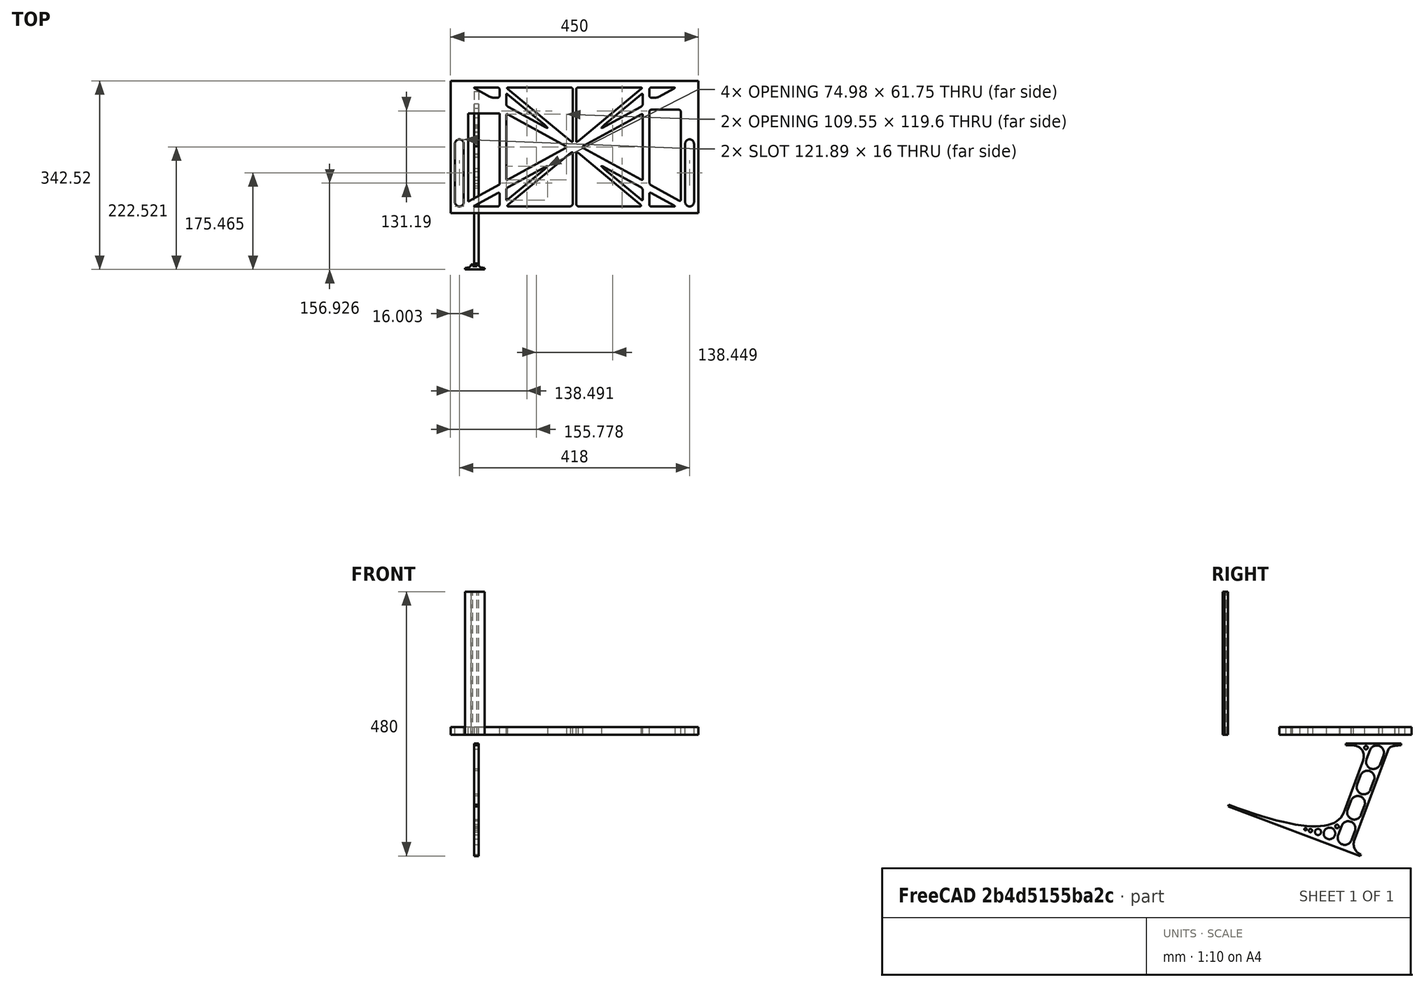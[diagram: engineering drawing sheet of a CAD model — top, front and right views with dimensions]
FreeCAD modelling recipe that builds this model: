
FCSTD DOCUMENT  (FreeCAD 0.19R0.19.2)
Label: laptopStand127FCStd
License: All rights reserved
LicenseURL: http://en.wikipedia.org/wiki/All_rights_reserved
objects: Sketcher::SketchObject×3, Part::Extrusion×3
note: 6 computed .brp shape members not serialized (recipe doc carries the construction recipe); baked Part::Feature solids carry a one-line shape summary decoded from their .brp

FEATURE [Sketcher::SketchObject] Sketch
  FullyConstrained = true
  sketch-geometry (352):
    g0: LineSegment StartX=-10.9272 StartY=-82.7794 StartZ=0 EndX=46.0728 EndY=-51.4823 EndZ=0
    g1: LineSegment StartX=-10.9272 StartY=76.4095 StartZ=0 EndX=-10.9272 EndY=-82.7794 EndZ=0
    g2: LineSegment StartX=46.0728 StartY=76.4095 StartZ=0 EndX=46.0728 EndY=-51.4823 EndZ=0
    g3: LineSegment StartX=-42.9272 StartY=136.221 StartZ=0 EndX=-42.9272 EndY=-103.779 EndZ=0
    g4: LineSegment StartX=407.073 StartY=136.221 StartZ=0 EndX=407.073 EndY=-103.779 EndZ=0
    g5: ArcOfCircle CenterX=-26.9272 CenterY=22.1087 CenterZ=0 NormalX=0 NormalY=0 NormalZ=1 AngleXU=0 Radius=8 StartAngle=1e-16 EndAngle=3.14159
    g6: ArcOfCircle CenterX=-26.9272 CenterY=-83.7794 CenterZ=0 NormalX=0 NormalY=0 NormalZ=1 AngleXU=0 Radius=8 StartAngle=3.14159 EndAngle=6.28319
    g7: LineSegment StartX=-34.9272 StartY=22.1087 StartZ=0 EndX=-34.9272 EndY=-83.7794 EndZ=0
    g8: LineSegment StartX=-18.9272 StartY=22.1087 StartZ=0 EndX=-18.9272 EndY=-83.7794 EndZ=0
    g9: ArcOfCircle CenterX=391.073 CenterY=22.1087 CenterZ=0 NormalX=0 NormalY=0 NormalZ=1 AngleXU=0 Radius=8 StartAngle=-4.4e-15 EndAngle=3.14159
    g10: LineSegment StartX=399.073 StartY=22.1087 StartZ=0 EndX=399.073 EndY=-83.7794 EndZ=0
    g11: LineSegment StartX=383.073 StartY=22.1087 StartZ=0 EndX=383.073 EndY=-83.7794 EndZ=0
    g12: ArcOfCircle CenterX=391.073 CenterY=-83.7794 CenterZ=0 NormalX=0 NormalY=0 NormalZ=1 AngleXU=0 Radius=8 StartAngle=3.14159 EndAngle=6.28319
    g13: Circle CenterX=175.022 CenterY=27.0628 CenterZ=0 NormalX=0 NormalY=0 NormalZ=1 AngleXU=0 Radius=1
    g14: Circle CenterX=179.022 CenterY=24.8665 CenterZ=0 NormalX=0 NormalY=0 NormalZ=1 AngleXU=0 Radius=1
    g15: Circle CenterX=179.022 CenterY=27.0628 CenterZ=0 NormalX=0 NormalY=0 NormalZ=1 AngleXU=0 Radius=1
    g16: BSplineCurve PolesCount=3 KnotsCount=2 Degree=2 IsPeriodic=0
    g17: GeomPoint X=175.022 Y=27.0628 Z=0
    g18: GeomPoint X=179.022 Y=27.0628 Z=0
    g19: Circle CenterX=189.124 CenterY=27.0628 CenterZ=0 NormalX=0 NormalY=0 NormalZ=1 AngleXU=0 Radius=1
    g20: Circle CenterX=185.124 CenterY=24.8665 CenterZ=0 NormalX=0 NormalY=0 NormalZ=1 AngleXU=0 Radius=1
    g21: Circle CenterX=185.124 CenterY=27.0628 CenterZ=0 NormalX=0 NormalY=0 NormalZ=1 AngleXU=0 Radius=1
    g22: BSplineCurve PolesCount=3 KnotsCount=2 Degree=2 IsPeriodic=0
    g23: GeomPoint X=189.124 Y=27.0628 Z=0
    g24: GeomPoint X=185.124 Y=27.0628 Z=0
    g25: Circle CenterX=175.022 CenterY=5.37834 CenterZ=0 NormalX=0 NormalY=0 NormalZ=1 AngleXU=0 Radius=1
    g26: Circle CenterX=179.022 CenterY=7.57463 CenterZ=0 NormalX=0 NormalY=0 NormalZ=1 AngleXU=0 Radius=1
    g27: Circle CenterX=179.022 CenterY=5.34704 CenterZ=0 NormalX=0 NormalY=0 NormalZ=1 AngleXU=0 Radius=1
    g28: BSplineCurve PolesCount=3 KnotsCount=2 Degree=2 IsPeriodic=0
    g29: GeomPoint X=175.022 Y=5.37834 Z=0
    g30: GeomPoint X=179.022 Y=5.34704 Z=0
    g31: Circle CenterX=189.124 CenterY=5.37834 CenterZ=0 NormalX=0 NormalY=0 NormalZ=1 AngleXU=0 Radius=1
    g32: Circle CenterX=185.124 CenterY=7.57463 CenterZ=0 NormalX=0 NormalY=0 NormalZ=1 AngleXU=0 Radius=1
    g33: Circle CenterX=185.124 CenterY=5.34704 CenterZ=0 NormalX=0 NormalY=0 NormalZ=1 AngleXU=0 Radius=1
    g34: BSplineCurve PolesCount=3 KnotsCount=2 Degree=2 IsPeriodic=0
    g35: GeomPoint X=189.124 Y=5.37834 Z=0
    g36: GeomPoint X=185.124 Y=5.34704 Z=0
    g37: Circle CenterX=165.871 CenterY=18.1458 CenterZ=0 NormalX=0 NormalY=0 NormalZ=1 AngleXU=0 Radius=1
    g38: Circle CenterX=169.377 CenterY=16.2206 CenterZ=0 NormalX=0 NormalY=0 NormalZ=1 AngleXU=0 Radius=1
    g39: Circle CenterX=165.871 CenterY=14.2954 CenterZ=0 NormalX=0 NormalY=0 NormalZ=1 AngleXU=0 Radius=1
    g40: BSplineCurve PolesCount=3 KnotsCount=2 Degree=2 IsPeriodic=0
    g41: GeomPoint X=165.871 Y=18.1458 Z=0
    g42: GeomPoint X=165.871 Y=14.2954 Z=0
    g43: Circle CenterX=198.275 CenterY=18.1458 CenterZ=0 NormalX=0 NormalY=0 NormalZ=1 AngleXU=0 Radius=1
    g44: Circle CenterX=194.768 CenterY=16.2206 CenterZ=0 NormalX=0 NormalY=0 NormalZ=1 AngleXU=0 Radius=1
    g45: Circle CenterX=198.275 CenterY=14.2954 CenterZ=0 NormalX=0 NormalY=0 NormalZ=1 AngleXU=0 Radius=1
    g46: BSplineCurve PolesCount=3 KnotsCount=2 Degree=2 IsPeriodic=0
    g47: GeomPoint X=198.275 Y=18.1458 Z=0
    g48: GeomPoint X=198.275 Y=14.2954 Z=0
    g49: LineSegment StartX=407.073 StartY=-103.779 StartZ=0 EndX=-42.9272 EndY=-103.779 EndZ=0
    g50: LineSegment StartX=407.073 StartY=136.221 StartZ=0 EndX=-42.9272 EndY=136.221 EndZ=0
    g51: LineSegment StartX=46.0728 StartY=76.4095 StartZ=0 EndX=-10.9272 EndY=76.4095 EndZ=0
    g52: Circle CenterX=125.607 CenterY=54.1951 CenterZ=0 NormalX=0 NormalY=0 NormalZ=1 AngleXU=0 Radius=1
    g53: Circle CenterX=139.632 CenterY=46.4944 CenterZ=0 NormalX=0 NormalY=0 NormalZ=1 AngleXU=0 Radius=1
    g54: Circle CenterX=127.326 CenterY=56.7187 CenterZ=0 NormalX=0 NormalY=0 NormalZ=1 AngleXU=0 Radius=1
    g55: BSplineCurve PolesCount=3 KnotsCount=2 Degree=2 IsPeriodic=0
    g56: GeomPoint X=125.607 Y=54.1951 Z=0
    g57: GeomPoint X=127.326 Y=56.7187 Z=0
    g58: Circle CenterX=236.821 CenterY=56.7187 CenterZ=0 NormalX=0 NormalY=0 NormalZ=1 AngleXU=0 Radius=1
    g59: Circle CenterX=224.513 CenterY=46.4944 CenterZ=0 NormalX=0 NormalY=0 NormalZ=1 AngleXU=0 Radius=1
    g60: Circle CenterX=238.538 CenterY=54.1951 CenterZ=0 NormalX=0 NormalY=0 NormalZ=1 AngleXU=0 Radius=1
    g61: BSplineCurve PolesCount=3 KnotsCount=2 Degree=2 IsPeriodic=0
    g62: GeomPoint X=236.821 Y=56.7187 Z=0
    g63: GeomPoint X=238.538 Y=54.1951 Z=0
    g64: Circle CenterX=238.538 CenterY=-21.7539 CenterZ=0 NormalX=0 NormalY=0 NormalZ=1 AngleXU=0 Radius=1
    g65: Circle CenterX=224.513 CenterY=-14.0532 CenterZ=0 NormalX=0 NormalY=0 NormalZ=1 AngleXU=0 Radius=1
    g66: Circle CenterX=236.821 CenterY=-24.2775 CenterZ=0 NormalX=0 NormalY=0 NormalZ=1 AngleXU=0 Radius=1
    g67: BSplineCurve PolesCount=3 KnotsCount=2 Degree=2 IsPeriodic=0
    g68: GeomPoint X=238.538 Y=-21.7539 Z=0
    g69: GeomPoint X=236.821 Y=-24.2775 Z=0
    g70: Circle CenterX=125.607 CenterY=-21.7539 CenterZ=0 NormalX=0 NormalY=0 NormalZ=1 AngleXU=0 Radius=1
    g71: Circle CenterX=139.632 CenterY=-14.0532 CenterZ=0 NormalX=0 NormalY=0 NormalZ=1 AngleXU=0 Radius=1
    g72: Circle CenterX=127.325 CenterY=-24.2775 CenterZ=0 NormalX=0 NormalY=0 NormalZ=1 AngleXU=0 Radius=1
    g73: BSplineCurve PolesCount=3 KnotsCount=2 Degree=2 IsPeriodic=0
    g74: GeomPoint X=125.607 Y=-21.7539 Z=0
    g75: GeomPoint X=127.325 Y=-24.2775 Z=0
    g76: Circle CenterX=302.996 CenterY=111.695 CenterZ=0 NormalX=0 NormalY=0 NormalZ=1 AngleXU=0 Radius=1
    g77: Circle CenterX=306.073 CenterY=114.251 CenterZ=0 NormalX=0 NormalY=0 NormalZ=1 AngleXU=0 Radius=1
    g78: Circle CenterX=306.073 CenterY=110.251 CenterZ=0 NormalX=0 NormalY=0 NormalZ=1 AngleXU=0 Radius=1
    g79: BSplineCurve PolesCount=3 KnotsCount=2 Degree=2 IsPeriodic=0
    g80: GeomPoint X=302.996 Y=111.695 Z=0
    g81: GeomPoint X=306.073 Y=110.251 Z=0
    g82: Circle CenterX=306.073 CenterY=95.2763 CenterZ=0 NormalX=0 NormalY=0 NormalZ=1 AngleXU=0 Radius=1
    g83: Circle CenterX=306.073 CenterY=91.2763 CenterZ=0 NormalX=0 NormalY=0 NormalZ=1 AngleXU=0 Radius=1
    g84: Circle CenterX=302.567 CenterY=89.3511 CenterZ=0 NormalX=0 NormalY=0 NormalZ=1 AngleXU=0 Radius=1
    g85: BSplineCurve PolesCount=3 KnotsCount=2 Degree=2 IsPeriodic=0
    g86: GeomPoint X=306.073 Y=95.2763 Z=0
    g87: GeomPoint X=302.567 Y=89.3511 Z=0
    g88: LineSegment StartX=306.073 StartY=110.251 StartZ=0 EndX=306.073 EndY=95.2763 EndZ=0
    g89: LineSegment StartX=302.996 StartY=111.695 StartZ=0 EndX=236.821 EndY=56.7187 EndZ=0
    g90: LineSegment StartX=238.538 StartY=54.1951 StartZ=0 EndX=302.567 EndY=89.3511 EndZ=0
    g91: Circle CenterX=61.1496 CenterY=111.695 CenterZ=0 NormalX=0 NormalY=0 NormalZ=1 AngleXU=0 Radius=1
    g92: Circle CenterX=58.0728 CenterY=114.251 CenterZ=0 NormalX=0 NormalY=0 NormalZ=1 AngleXU=0 Radius=1
    g93: Circle CenterX=58.0728 CenterY=110.251 CenterZ=0 NormalX=0 NormalY=0 NormalZ=1 AngleXU=0 Radius=1
    g94: BSplineCurve PolesCount=3 KnotsCount=2 Degree=2 IsPeriodic=0
    g95: GeomPoint X=61.1496 Y=111.695 Z=0
    g96: GeomPoint X=58.0728 Y=110.251 Z=0
    g97: Circle CenterX=61.5791 CenterY=89.3511 CenterZ=0 NormalX=0 NormalY=0 NormalZ=1 AngleXU=0 Radius=1
    g98: Circle CenterX=58.0728 CenterY=91.2763 CenterZ=0 NormalX=0 NormalY=0 NormalZ=1 AngleXU=0 Radius=1
    g99: Circle CenterX=58.0728 CenterY=95.2763 CenterZ=0 NormalX=0 NormalY=0 NormalZ=1 AngleXU=0 Radius=1
    g100: BSplineCurve PolesCount=3 KnotsCount=2 Degree=2 IsPeriodic=0
    g101: GeomPoint X=61.5791 Y=89.3511 Z=0
    g102: GeomPoint X=58.0728 Y=95.2763 Z=0
    g103: LineSegment StartX=58.0728 StartY=110.251 StartZ=0 EndX=58.0728 EndY=95.2763 EndZ=0
    g104: LineSegment StartX=61.1496 StartY=111.695 StartZ=0 EndX=127.326 EndY=56.7187 EndZ=0
    g105: LineSegment StartX=125.607 StartY=54.1951 StartZ=0 EndX=61.5791 EndY=89.3511 EndZ=0
    g106: Circle CenterX=61.5791 CenterY=-56.9099 CenterZ=0 NormalX=0 NormalY=0 NormalZ=1 AngleXU=0 Radius=1
    g107: Circle CenterX=58.0728 CenterY=-58.8351 CenterZ=0 NormalX=0 NormalY=0 NormalZ=1 AngleXU=0 Radius=1
    g108: Circle CenterX=58.0728 CenterY=-62.8351 CenterZ=0 NormalX=0 NormalY=0 NormalZ=1 AngleXU=0 Radius=1
    g109: BSplineCurve PolesCount=3 KnotsCount=2 Degree=2 IsPeriodic=0
    g110: GeomPoint X=61.5791 Y=-56.9099 Z=0
    g111: GeomPoint X=58.0728 Y=-62.8351 Z=0
    g112: Circle CenterX=58.0728 CenterY=-77.8102 CenterZ=0 NormalX=0 NormalY=0 NormalZ=1 AngleXU=0 Radius=1
    g113: Circle CenterX=58.0728 CenterY=-81.8102 CenterZ=0 NormalX=0 NormalY=0 NormalZ=1 AngleXU=0 Radius=1
    g114: Circle CenterX=61.1496 CenterY=-79.2541 CenterZ=0 NormalX=0 NormalY=0 NormalZ=1 AngleXU=0 Radius=1
    g115: BSplineCurve PolesCount=3 KnotsCount=2 Degree=2 IsPeriodic=0
    g116: GeomPoint X=58.0728 Y=-77.8102 Z=0
    g117: GeomPoint X=61.1496 Y=-79.2541 Z=0
    g118: LineSegment StartX=58.0728 StartY=-62.8351 StartZ=0 EndX=58.0728 EndY=-77.8102 EndZ=0
    g119: LineSegment StartX=61.1496 StartY=-79.2541 StartZ=0 EndX=127.325 EndY=-24.2775 EndZ=0
    g120: LineSegment StartX=125.607 StartY=-21.7539 StartZ=0 EndX=61.5791 EndY=-56.9099 EndZ=0
    g121: Circle CenterX=302.567 CenterY=-56.9099 CenterZ=0 NormalX=0 NormalY=0 NormalZ=1 AngleXU=0 Radius=1
    g122: Circle CenterX=306.073 CenterY=-58.8351 CenterZ=0 NormalX=0 NormalY=0 NormalZ=1 AngleXU=0 Radius=1
    g123: Circle CenterX=306.073 CenterY=-62.8351 CenterZ=0 NormalX=0 NormalY=0 NormalZ=1 AngleXU=0 Radius=1
    g124: BSplineCurve PolesCount=3 KnotsCount=2 Degree=2 IsPeriodic=0
    g125: GeomPoint X=302.567 Y=-56.9099 Z=0
    g126: GeomPoint X=306.073 Y=-62.8351 Z=0
    g127: Circle CenterX=302.996 CenterY=-79.2541 CenterZ=0 NormalX=0 NormalY=0 NormalZ=1 AngleXU=0 Radius=1
    g128: Circle CenterX=306.073 CenterY=-81.8102 CenterZ=0 NormalX=0 NormalY=0 NormalZ=1 AngleXU=0 Radius=1
    g129: Circle CenterX=306.073 CenterY=-77.8102 CenterZ=0 NormalX=0 NormalY=0 NormalZ=1 AngleXU=0 Radius=1
    g130: BSplineCurve PolesCount=3 KnotsCount=2 Degree=2 IsPeriodic=0
    g131: GeomPoint X=302.996 Y=-79.2541 Z=0
    g132: GeomPoint X=306.073 Y=-77.8102 Z=0
    g133: LineSegment StartX=306.073 StartY=-62.8351 StartZ=0 EndX=306.073 EndY=-77.8102 EndZ=0
    g134: LineSegment StartX=302.996 StartY=-79.2541 StartZ=0 EndX=236.821 EndY=-24.2775 EndZ=0
    g135: LineSegment StartX=238.538 StartY=-21.7539 StartZ=0 EndX=302.567 EndY=-56.9099 EndZ=0
    g136: Circle CenterX=61.6457 CenterY=-88.8112 CenterZ=0 NormalX=0 NormalY=0 NormalZ=1 AngleXU=0 Radius=1
    g137: Circle CenterX=58.0728 CenterY=-91.7794 CenterZ=0 NormalX=0 NormalY=0 NormalZ=1 AngleXU=0 Radius=1
    g138: Circle CenterX=63.9135 CenterY=-91.7794 CenterZ=0 NormalX=0 NormalY=0 NormalZ=1 AngleXU=0 Radius=1
    g139: BSplineCurve PolesCount=3 KnotsCount=2 Degree=2 IsPeriodic=0
    g140: GeomPoint X=61.6457 Y=-88.8112 Z=0
    g141: GeomPoint X=63.9135 Y=-91.7794 Z=0
    g142: Circle CenterX=179.022 CenterY=-85.8163 CenterZ=0 NormalX=0 NormalY=0 NormalZ=1 AngleXU=0 Radius=1
    g143: Circle CenterX=179.022 CenterY=-91.7794 CenterZ=0 NormalX=0 NormalY=0 NormalZ=1 AngleXU=0 Radius=1
    g144: Circle CenterX=171.895 CenterY=-91.7794 CenterZ=0 NormalX=0 NormalY=0 NormalZ=1 AngleXU=0 Radius=1
    g145: BSplineCurve PolesCount=3 KnotsCount=2 Degree=2 IsPeriodic=0
    g146: GeomPoint X=179.022 Y=-85.8163 Z=0
    g147: GeomPoint X=171.895 Y=-91.7794 Z=0
    g148: Circle CenterX=185.124 CenterY=-86.2028 CenterZ=0 NormalX=0 NormalY=0 NormalZ=1 AngleXU=0 Radius=1
    g149: Circle CenterX=185.124 CenterY=-91.7794 CenterZ=0 NormalX=0 NormalY=0 NormalZ=1 AngleXU=0 Radius=1
    g150: Circle CenterX=191.747 CenterY=-91.7794 CenterZ=0 NormalX=0 NormalY=0 NormalZ=1 AngleXU=0 Radius=1
    g151: BSplineCurve PolesCount=3 KnotsCount=2 Degree=2 IsPeriodic=0
    g152: GeomPoint X=185.124 Y=-86.2028 Z=0
    g153: GeomPoint X=191.747 Y=-91.7794 Z=0
    g154: Circle CenterX=299.888 CenterY=-86.6413 CenterZ=0 NormalX=0 NormalY=0 NormalZ=1 AngleXU=0 Radius=1
    g155: Circle CenterX=306.073 CenterY=-91.7794 CenterZ=0 NormalX=0 NormalY=0 NormalZ=1 AngleXU=0 Radius=1
    g156: Circle CenterX=298.776 CenterY=-91.7794 CenterZ=0 NormalX=0 NormalY=0 NormalZ=1 AngleXU=0 Radius=1
    g157: BSplineCurve PolesCount=3 KnotsCount=2 Degree=2 IsPeriodic=0
    g158: GeomPoint X=299.888 Y=-86.6413 Z=0
    g159: GeomPoint X=298.776 Y=-91.7794 Z=0
    g160: LineSegment StartX=189.124 StartY=5.37834 StartZ=0 EndX=299.888 EndY=-86.6413 EndZ=0
    g161: LineSegment StartX=298.776 StartY=-91.7794 StartZ=0 EndX=191.747 EndY=-91.7794 EndZ=0
    g162: LineSegment StartX=185.124 StartY=-86.2028 StartZ=0 EndX=185.124 EndY=5.34704 EndZ=0
    g163: LineSegment StartX=179.022 StartY=5.34704 StartZ=0 EndX=179.022 EndY=-85.8163 EndZ=0
    g164: LineSegment StartX=171.895 StartY=-91.7794 StartZ=0 EndX=63.9135 EndY=-91.7794 EndZ=0
    g165: LineSegment StartX=61.6457 StartY=-88.8112 StartZ=0 EndX=175.022 EndY=5.37834 EndZ=0
    g166: Circle CenterX=302.073 CenterY=124.221 CenterZ=0 NormalX=0 NormalY=0 NormalZ=1 AngleXU=0 Radius=1
    g167: Circle CenterX=306.073 CenterY=124.221 CenterZ=0 NormalX=0 NormalY=0 NormalZ=1 AngleXU=0 Radius=1
    g168: Circle CenterX=302.996 CenterY=121.665 CenterZ=0 NormalX=0 NormalY=0 NormalZ=1 AngleXU=0 Radius=1
    g169: BSplineCurve PolesCount=3 KnotsCount=2 Degree=2 IsPeriodic=0
    g170: GeomPoint X=302.073 Y=124.221 Z=0
    g171: GeomPoint X=302.996 Y=121.665 Z=0
    g172: Circle CenterX=189.124 CenterY=124.221 CenterZ=0 NormalX=0 NormalY=0 NormalZ=1 AngleXU=0 Radius=1
    g173: Circle CenterX=185.124 CenterY=124.221 CenterZ=0 NormalX=0 NormalY=0 NormalZ=1 AngleXU=0 Radius=1
    g174: Circle CenterX=185.124 CenterY=120.221 CenterZ=0 NormalX=0 NormalY=0 NormalZ=1 AngleXU=0 Radius=1
    g175: BSplineCurve PolesCount=3 KnotsCount=2 Degree=2 IsPeriodic=0
    g176: GeomPoint X=189.124 Y=124.221 Z=0
    g177: GeomPoint X=185.124 Y=120.221 Z=0
    g178: Circle CenterX=175.022 CenterY=124.221 CenterZ=0 NormalX=0 NormalY=0 NormalZ=1 AngleXU=0 Radius=1
    g179: Circle CenterX=179.022 CenterY=124.221 CenterZ=0 NormalX=0 NormalY=0 NormalZ=1 AngleXU=0 Radius=1
    g180: Circle CenterX=179.022 CenterY=120.221 CenterZ=0 NormalX=0 NormalY=0 NormalZ=1 AngleXU=0 Radius=1
    g181: BSplineCurve PolesCount=3 KnotsCount=2 Degree=2 IsPeriodic=0
    g182: GeomPoint X=175.022 Y=124.221 Z=0
    g183: GeomPoint X=179.022 Y=120.221 Z=0
    g184: Circle CenterX=62.0728 CenterY=124.221 CenterZ=0 NormalX=0 NormalY=0 NormalZ=1 AngleXU=0 Radius=1
    g185: Circle CenterX=58.0728 CenterY=124.221 CenterZ=0 NormalX=0 NormalY=0 NormalZ=1 AngleXU=0 Radius=1
    g186: Circle CenterX=61.1496 CenterY=121.665 CenterZ=0 NormalX=0 NormalY=0 NormalZ=1 AngleXU=0 Radius=1
    g187: BSplineCurve PolesCount=3 KnotsCount=2 Degree=2 IsPeriodic=0
    g188: GeomPoint X=62.0728 Y=124.221 Z=0
    g189: GeomPoint X=61.1496 Y=121.665 Z=0
    g190: LineSegment StartX=62.0728 StartY=124.221 StartZ=0 EndX=175.022 EndY=124.221 EndZ=0
    g191: LineSegment StartX=179.022 StartY=120.221 StartZ=0 EndX=179.022 EndY=27.0628 EndZ=0
    g192: LineSegment StartX=185.124 StartY=27.0628 StartZ=0 EndX=185.124 EndY=120.221 EndZ=0
    g193: LineSegment StartX=189.124 StartY=124.221 StartZ=0 EndX=302.073 EndY=124.221 EndZ=0
    g194: LineSegment StartX=302.996 StartY=121.665 StartZ=0 EndX=189.124 EndY=27.0628 EndZ=0
    g195: LineSegment StartX=175.022 StartY=27.0628 StartZ=0 EndX=61.1496 EndY=121.665 EndZ=0
    g196: Circle CenterX=61.5791 CenterY=75.4095 CenterZ=0 NormalX=0 NormalY=0 NormalZ=1 AngleXU=0 Radius=1
    g197: Circle CenterX=58.0728 CenterY=77.3346 CenterZ=0 NormalX=0 NormalY=0 NormalZ=1 AngleXU=0 Radius=1
    g198: Circle CenterX=58.0728 CenterY=73.3346 CenterZ=0 NormalX=0 NormalY=0 NormalZ=1 AngleXU=0 Radius=1
    g199: BSplineCurve PolesCount=3 KnotsCount=2 Degree=2 IsPeriodic=0
    g200: GeomPoint X=61.5791 Y=75.4095 Z=0
    g201: GeomPoint X=58.0728 Y=73.3346 Z=0
    g202: Circle CenterX=58.0728 CenterY=-40.8935 CenterZ=0 NormalX=0 NormalY=0 NormalZ=1 AngleXU=0 Radius=1
    g203: Circle CenterX=58.0728 CenterY=-44.8935 CenterZ=0 NormalX=0 NormalY=0 NormalZ=1 AngleXU=0 Radius=1
    g204: Circle CenterX=61.5791 CenterY=-42.9683 CenterZ=0 NormalX=0 NormalY=0 NormalZ=1 AngleXU=0 Radius=1
    g205: BSplineCurve PolesCount=3 KnotsCount=2 Degree=2 IsPeriodic=0
    g206: GeomPoint X=58.0728 Y=-40.8935 Z=0
    g207: GeomPoint X=61.5791 Y=-42.9683 Z=0
    g208: LineSegment StartX=61.5791 StartY=-42.9683 StartZ=0 EndX=165.871 EndY=14.2954 EndZ=0
    g209: LineSegment StartX=165.871 StartY=18.1458 StartZ=0 EndX=61.5791 EndY=75.4095 EndZ=0
    g210: LineSegment StartX=58.0728 StartY=73.3346 StartZ=0 EndX=58.0728 EndY=-40.8935 EndZ=0
    g211: Circle CenterX=302.567 CenterY=-42.9683 CenterZ=0 NormalX=0 NormalY=0 NormalZ=1 AngleXU=0 Radius=1
    g212: Circle CenterX=306.073 CenterY=-44.8935 CenterZ=0 NormalX=0 NormalY=0 NormalZ=1 AngleXU=0 Radius=1
    g213: Circle CenterX=306.073 CenterY=-40.8935 CenterZ=0 NormalX=0 NormalY=0 NormalZ=1 AngleXU=0 Radius=1
    g214: BSplineCurve PolesCount=3 KnotsCount=2 Degree=2 IsPeriodic=0
    g215: GeomPoint X=302.567 Y=-42.9683 Z=0
    g216: GeomPoint X=306.073 Y=-40.8935 Z=0
    g217: Circle CenterX=306.073 CenterY=73.3346 CenterZ=0 NormalX=0 NormalY=0 NormalZ=1 AngleXU=0 Radius=1
    g218: Circle CenterX=306.073 CenterY=77.3346 CenterZ=0 NormalX=0 NormalY=0 NormalZ=1 AngleXU=0 Radius=1
    g219: Circle CenterX=302.567 CenterY=75.4095 CenterZ=0 NormalX=0 NormalY=0 NormalZ=1 AngleXU=0 Radius=1
    g220: BSplineCurve PolesCount=3 KnotsCount=2 Degree=2 IsPeriodic=0
    g221: GeomPoint X=306.073 Y=73.3346 Z=0
    g222: GeomPoint X=302.567 Y=75.4095 Z=0
    g223: LineSegment StartX=302.567 StartY=-42.9683 StartZ=0 EndX=198.275 EndY=14.2954 EndZ=0
    g224: LineSegment StartX=198.275 StartY=18.1458 StartZ=0 EndX=302.567 EndY=75.4095 EndZ=0
    g225: LineSegment StartX=306.073 StartY=73.3346 StartZ=0 EndX=306.073 EndY=-40.8935 EndZ=0
    g226: LineSegment StartX=322.073 StartY=105.865 StartZ=0 EndX=328.643 EndY=105.865 EndZ=0
    g227: LineSegment StartX=318.073 StartY=120.221 StartZ=0 EndX=318.073 EndY=109.865 EndZ=0
    g228: LineSegment StartX=336.157 StartY=107.779 StartZ=0 EndX=362.567 EndY=122.294 EndZ=0
    g229: Circle CenterX=362.073 CenterY=124.221 CenterZ=0 NormalX=0 NormalY=0 NormalZ=1 AngleXU=0 Radius=1
    g230: Circle CenterX=366.073 CenterY=124.221 CenterZ=0 NormalX=0 NormalY=0 NormalZ=1 AngleXU=0 Radius=1
    g231: Circle CenterX=362.567 CenterY=122.294 CenterZ=0 NormalX=0 NormalY=0 NormalZ=1 AngleXU=0 Radius=1
    g232: BSplineCurve PolesCount=3 KnotsCount=2 Degree=2 IsPeriodic=0
    g233: GeomPoint X=362.073 Y=124.221 Z=0
    g234: GeomPoint X=362.567 Y=122.294 Z=0
    g235: Circle CenterX=322.073 CenterY=124.221 CenterZ=0 NormalX=0 NormalY=0 NormalZ=1 AngleXU=0 Radius=1
    g236: Circle CenterX=318.073 CenterY=124.221 CenterZ=0 NormalX=0 NormalY=0 NormalZ=1 AngleXU=0 Radius=1
    g237: Circle CenterX=318.073 CenterY=120.221 CenterZ=0 NormalX=0 NormalY=0 NormalZ=1 AngleXU=0 Radius=1
    g238: BSplineCurve PolesCount=3 KnotsCount=2 Degree=2 IsPeriodic=0
    g239: GeomPoint X=322.073 Y=124.221 Z=0
    g240: GeomPoint X=318.073 Y=120.221 Z=0
    g241: Circle CenterX=322.073 CenterY=105.865 CenterZ=0 NormalX=0 NormalY=0 NormalZ=1 AngleXU=0 Radius=1
    g242: Circle CenterX=318.073 CenterY=105.865 CenterZ=0 NormalX=0 NormalY=0 NormalZ=1 AngleXU=0 Radius=1
    g243: Circle CenterX=318.073 CenterY=109.865 CenterZ=0 NormalX=0 NormalY=0 NormalZ=1 AngleXU=0 Radius=1
    g244: BSplineCurve PolesCount=3 KnotsCount=2 Degree=2 IsPeriodic=0
    g245: GeomPoint X=322.073 Y=105.865 Z=0
    g246: GeomPoint X=318.073 Y=109.865 Z=0
    g247: Circle CenterX=336.157 CenterY=107.779 CenterZ=0 NormalX=0 NormalY=0 NormalZ=1 AngleXU=0 Radius=1
    g248: Circle CenterX=332.651 CenterY=105.853 CenterZ=0 NormalX=0 NormalY=0 NormalZ=1 AngleXU=0 Radius=1
    g249: Circle CenterX=328.643 CenterY=105.865 CenterZ=0 NormalX=0 NormalY=0 NormalZ=1 AngleXU=0 Radius=1
    g250: BSplineCurve PolesCount=3 KnotsCount=2 Degree=2 IsPeriodic=0
    g251: GeomPoint X=336.157 Y=107.779 Z=0
    g252: GeomPoint X=328.643 Y=105.865 Z=0
    g253: LineSegment StartX=322.073 StartY=124.221 StartZ=0 EndX=362.073 EndY=124.221 EndZ=0
    g254: Circle CenterX=371.567 CenterY=-80.8644 CenterZ=0 NormalX=0 NormalY=0 NormalZ=1 AngleXU=0 Radius=1
    g255: Circle CenterX=375.073 CenterY=-82.7896 CenterZ=0 NormalX=0 NormalY=0 NormalZ=1 AngleXU=0 Radius=1
    g256: Circle CenterX=375.073 CenterY=-78.7896 CenterZ=0 NormalX=0 NormalY=0 NormalZ=1 AngleXU=0 Radius=1
    g257: BSplineCurve PolesCount=3 KnotsCount=2 Degree=2 IsPeriodic=0
    g258: GeomPoint X=371.567 Y=-80.8644 Z=0
    g259: GeomPoint X=375.073 Y=-78.7896 Z=0
    g260: Circle CenterX=321.579 CenterY=-53.4075 CenterZ=0 NormalX=0 NormalY=0 NormalZ=1 AngleXU=0 Radius=1
    g261: Circle CenterX=318.073 CenterY=-51.4823 CenterZ=0 NormalX=0 NormalY=0 NormalZ=1 AngleXU=0 Radius=1
    g262: Circle CenterX=318.073 CenterY=-47.4823 CenterZ=0 NormalX=0 NormalY=0 NormalZ=1 AngleXU=0 Radius=1
    g263: BSplineCurve PolesCount=3 KnotsCount=2 Degree=2 IsPeriodic=0
    g264: GeomPoint X=321.579 Y=-53.4075 Z=0
    g265: GeomPoint X=318.073 Y=-47.4823 Z=0
    g266: Circle CenterX=318.073 CenterY=79.9235 CenterZ=0 NormalX=0 NormalY=0 NormalZ=1 AngleXU=0 Radius=1
    g267: Circle CenterX=318.073 CenterY=83.9235 CenterZ=0 NormalX=0 NormalY=0 NormalZ=1 AngleXU=0 Radius=1
    g268: Circle CenterX=322.073 CenterY=83.9235 CenterZ=0 NormalX=0 NormalY=0 NormalZ=1 AngleXU=0 Radius=1
    g269: BSplineCurve PolesCount=3 KnotsCount=2 Degree=2 IsPeriodic=0
    g270: GeomPoint X=318.073 Y=79.9235 Z=0
    g271: GeomPoint X=322.073 Y=83.9235 Z=0
    g272: Circle CenterX=375.073 CenterY=79.9235 CenterZ=0 NormalX=0 NormalY=0 NormalZ=1 AngleXU=0 Radius=1
    g273: Circle CenterX=375.073 CenterY=83.9235 CenterZ=0 NormalX=0 NormalY=0 NormalZ=1 AngleXU=0 Radius=1
    g274: Circle CenterX=371.073 CenterY=83.9235 CenterZ=0 NormalX=0 NormalY=0 NormalZ=1 AngleXU=0 Radius=1
    g275: BSplineCurve PolesCount=3 KnotsCount=2 Degree=2 IsPeriodic=0
    g276: GeomPoint X=375.073 Y=79.9235 Z=0
    g277: GeomPoint X=371.073 Y=83.9235 Z=0
    g278: LineSegment StartX=322.073 StartY=83.9235 StartZ=0 EndX=371.073 EndY=83.9235 EndZ=0
    g279: LineSegment StartX=375.073 StartY=79.9235 StartZ=0 EndX=375.073 EndY=-78.7896 EndZ=0
    g280: LineSegment StartX=371.567 StartY=-80.8644 StartZ=0 EndX=321.579 EndY=-53.4075 EndZ=0
    g281: LineSegment StartX=318.073 StartY=-47.4823 StartZ=0 EndX=318.073 EndY=79.9235 EndZ=0
    g282: Circle CenterX=321.579 CenterY=-67.3492 CenterZ=0 NormalX=0 NormalY=0 NormalZ=1 AngleXU=0 Radius=1
    g283: Circle CenterX=318.073 CenterY=-65.424 CenterZ=0 NormalX=0 NormalY=0 NormalZ=1 AngleXU=0 Radius=1
    g284: Circle CenterX=318.073 CenterY=-69.424 CenterZ=0 NormalX=0 NormalY=0 NormalZ=1 AngleXU=0 Radius=1
    g285: BSplineCurve PolesCount=3 KnotsCount=2 Degree=2 IsPeriodic=0
    g286: GeomPoint X=321.579 Y=-67.3492 Z=0
    g287: GeomPoint X=318.073 Y=-69.424 Z=0
    g288: Circle CenterX=362.567 CenterY=-89.8542 CenterZ=0 NormalX=0 NormalY=0 NormalZ=1 AngleXU=0 Radius=1
    g289: Circle CenterX=366.073 CenterY=-91.7794 CenterZ=0 NormalX=0 NormalY=0 NormalZ=1 AngleXU=0 Radius=1
    g290: Circle CenterX=362.073 CenterY=-91.7794 CenterZ=0 NormalX=0 NormalY=0 NormalZ=1 AngleXU=0 Radius=1
    g291: BSplineCurve PolesCount=3 KnotsCount=2 Degree=2 IsPeriodic=0
    g292: GeomPoint X=362.567 Y=-89.8542 Z=0
    g293: GeomPoint X=362.073 Y=-91.7794 Z=0
    g294: Circle CenterX=322.073 CenterY=-91.7794 CenterZ=0 NormalX=0 NormalY=0 NormalZ=1 AngleXU=0 Radius=1
    g295: Circle CenterX=318.073 CenterY=-91.7794 CenterZ=0 NormalX=0 NormalY=0 NormalZ=1 AngleXU=0 Radius=1
    g296: Circle CenterX=318.073 CenterY=-87.7794 CenterZ=0 NormalX=0 NormalY=0 NormalZ=1 AngleXU=0 Radius=1
    g297: BSplineCurve PolesCount=3 KnotsCount=2 Degree=2 IsPeriodic=0
    g298: GeomPoint X=322.073 Y=-91.7794 Z=0
    g299: GeomPoint X=318.073 Y=-87.7794 Z=0
    g300: LineSegment StartX=362.567 StartY=-89.8542 StartZ=0 EndX=321.579 EndY=-67.3492 EndZ=0
    g301: LineSegment StartX=318.073 StartY=-69.424 StartZ=0 EndX=318.073 EndY=-87.7794 EndZ=0
    g302: LineSegment StartX=322.073 StartY=-91.7794 StartZ=0 EndX=362.073 EndY=-91.7794 EndZ=0
    g303: Circle CenterX=2.07281 CenterY=124.221 CenterZ=0 NormalX=0 NormalY=0 NormalZ=1 AngleXU=0 Radius=1
    g304: Circle CenterX=1.57905 CenterY=122.295 CenterZ=0 NormalX=0 NormalY=0 NormalZ=1 AngleXU=0 Radius=1
    g305: BSplineCurve PolesCount=3 KnotsCount=2 Degree=2 IsPeriodic=0
    g306: GeomPoint X=2.07281 Y=124.221 Z=0
    g307: GeomPoint X=1.57905 Y=122.295 Z=0
    g308: Circle CenterX=42.0728 CenterY=124.221 CenterZ=0 NormalX=0 NormalY=0 NormalZ=1 AngleXU=0 Radius=1
    g309: Circle CenterX=46.0728 CenterY=124.221 CenterZ=0 NormalX=0 NormalY=0 NormalZ=1 AngleXU=0 Radius=1
    g310: Circle CenterX=46.0728 CenterY=120.221 CenterZ=0 NormalX=0 NormalY=0 NormalZ=1 AngleXU=0 Radius=1
    g311: BSplineCurve PolesCount=3 KnotsCount=2 Degree=2 IsPeriodic=0
    g312: GeomPoint X=42.0728 Y=124.221 Z=0
    g313: GeomPoint X=46.0728 Y=120.221 Z=0
    g314: Circle CenterX=46.0728 CenterY=109.865 CenterZ=0 NormalX=0 NormalY=0 NormalZ=1 AngleXU=0 Radius=1
    g315: Circle CenterX=46.0728 CenterY=105.865 CenterZ=0 NormalX=0 NormalY=0 NormalZ=1 AngleXU=0 Radius=1
    g316: Circle CenterX=42.0728 CenterY=105.865 CenterZ=0 NormalX=0 NormalY=0 NormalZ=1 AngleXU=0 Radius=1
    g317: BSplineCurve PolesCount=3 KnotsCount=2 Degree=2 IsPeriodic=0
    g318: GeomPoint X=46.0728 Y=109.865 Z=0
    g319: GeomPoint X=42.0728 Y=105.865 Z=0
    g320: Circle CenterX=35.5028 CenterY=105.865 CenterZ=0 NormalX=0 NormalY=0 NormalZ=1 AngleXU=0 Radius=1
    g321: Circle CenterX=31.5028 CenterY=105.865 CenterZ=0 NormalX=0 NormalY=0 NormalZ=1 AngleXU=0 Radius=1
    g322: Circle CenterX=27.9965 CenterY=107.79 CenterZ=0 NormalX=0 NormalY=0 NormalZ=1 AngleXU=0 Radius=1
    g323: BSplineCurve PolesCount=3 KnotsCount=2 Degree=2 IsPeriodic=0
    g324: GeomPoint X=35.5028 Y=105.865 Z=0
    g325: GeomPoint X=27.9965 Y=107.79 Z=0
    g326: LineSegment StartX=2.07281 StartY=124.221 StartZ=0 EndX=42.0728 EndY=124.221 EndZ=0
    g327: LineSegment StartX=46.0728 StartY=120.221 StartZ=0 EndX=46.0728 EndY=109.865 EndZ=0
    g328: LineSegment StartX=42.0728 StartY=105.865 StartZ=0 EndX=35.5028 EndY=105.865 EndZ=0
    g329: LineSegment StartX=27.9965 StartY=107.79 StartZ=0 EndX=1.57905 EndY=122.295 EndZ=0
    g330: Circle CenterX=42.5666 CenterY=-67.3492 CenterZ=0 NormalX=0 NormalY=0 NormalZ=1 AngleXU=0 Radius=1
    g331: Circle CenterX=46.0728 CenterY=-65.424 CenterZ=0 NormalX=0 NormalY=0 NormalZ=1 AngleXU=0 Radius=1
    g332: Circle CenterX=46.0728 CenterY=-69.424 CenterZ=0 NormalX=0 NormalY=0 NormalZ=1 AngleXU=0 Radius=1
    g333: BSplineCurve PolesCount=3 KnotsCount=2 Degree=2 IsPeriodic=0
    g334: GeomPoint X=42.5666 Y=-67.3492 Z=0
    g335: GeomPoint X=46.0728 Y=-69.424 Z=0
    g336: Circle CenterX=46.0728 CenterY=-87.7794 CenterZ=0 NormalX=0 NormalY=0 NormalZ=1 AngleXU=0 Radius=1
    g337: Circle CenterX=46.0728 CenterY=-91.7794 CenterZ=0 NormalX=0 NormalY=0 NormalZ=1 AngleXU=0 Radius=1
    g338: Circle CenterX=42.0728 CenterY=-91.7794 CenterZ=0 NormalX=0 NormalY=0 NormalZ=1 AngleXU=0 Radius=1
    g339: BSplineCurve PolesCount=3 KnotsCount=2 Degree=2 IsPeriodic=0
    g340: GeomPoint X=46.0728 Y=-87.7794 Z=0
    g341: GeomPoint X=42.0728 Y=-91.7794 Z=0
    g342: Circle CenterX=2.07281 CenterY=-91.7794 CenterZ=0 NormalX=0 NormalY=0 NormalZ=1 AngleXU=0 Radius=1
    g343: Circle CenterX=-1.92719 CenterY=-91.7794 CenterZ=0 NormalX=0 NormalY=0 NormalZ=1 AngleXU=0 Radius=1
    g344: Circle CenterX=1.57905 CenterY=-89.8542 CenterZ=0 NormalX=0 NormalY=0 NormalZ=1 AngleXU=0 Radius=1
    g345: BSplineCurve PolesCount=3 KnotsCount=2 Degree=2 IsPeriodic=0
    g346: GeomPoint X=2.07281 Y=-91.7794 Z=0
    g347: GeomPoint X=1.57905 Y=-89.8542 Z=0
    g348: LineSegment StartX=2.07281 StartY=-91.7794 StartZ=0 EndX=42.0728 EndY=-91.7794 EndZ=0
    g349: LineSegment StartX=46.0728 StartY=-87.7794 StartZ=0 EndX=46.0728 EndY=-69.424 EndZ=0
    g350: LineSegment StartX=42.5666 StartY=-67.3492 StartZ=0 EndX=1.57905 EndY=-89.8542 EndZ=0
    g351: LineSegment StartX=318.073 StartY=76.4095 StartZ=0 EndX=375.073 EndY=76.4095 EndZ=0
  constraints (585):
    c: Coincident(g0,g2)
    c: Block(g0)
    c: Block(g1)
    c: Vertical(g3)
    c: Vertical(g4)
    c: Block(g4)
    c: Block(g3)
    c: Tangent(g5,g8) = 1.5708
    c: Tangent(g5,g7) = -1.5708
    c: Tangent(g7,g6) = -1.5708
    c: Tangent(g8,g6) = 1.5708
    c: Vertical(g7)
    c: Equal(g5,g6)
    c: Block(g8)
    c: Block(g7)
    c: Tangent(g9,g10) = 1.5708
    c: Tangent(g10,g12) = 1.5708
    c: Equal(g9,g12)
    c: Coincident(g11,g9)
    c: Coincident(g11,g12)
    c: Block(g10)
    c: Block(g11)
    c: Weight(g13) = 1
    c: Equal(g13,g14)
    c: Equal(g13,g15)
    c: InternalAlignment(g13,g16)
    c: InternalAlignment(g14,g16)
    c: InternalAlignment(g15,g16)
    c: InternalAlignment(g17,g16)
    c: InternalAlignment(g18,g16)
    c: Weight(g19) = 1
    c: Equal(g19,g20)
    c: Equal(g19,g21)
    c: InternalAlignment(g19,g22)
    c: InternalAlignment(g20,g22)
    c: InternalAlignment(g21,g22)
    c: InternalAlignment(g23,g22)
    c: InternalAlignment(g24,g22)
    c: Block(g22)
    c: Block(g16)
    c: Weight(g25) = 1
    c: Equal(g25,g26)
    c: Equal(g25,g27)
    c: InternalAlignment(g25,g28)
    c: InternalAlignment(g26,g28)
    c: InternalAlignment(g27,g28)
    c: InternalAlignment(g29,g28)
    c: InternalAlignment(g30,g28)
    c: Weight(g31) = 1
    c: Equal(g31,g32)
    c: Equal(g31,g33)
    c: InternalAlignment(g31,g34)
    c: InternalAlignment(g32,g34)
    c: InternalAlignment(g33,g34)
    c: InternalAlignment(g35,g34)
    c: InternalAlignment(g36,g34)
    c: Block(g34)
    c: Block(g28)
    c: Weight(g37) = 1
    c: Equal(g37,g38)
    c: Equal(g37,g39)
    c: InternalAlignment(g37,g40)
    c: InternalAlignment(g38,g40)
    c: InternalAlignment(g39,g40)
    c: InternalAlignment(g41,g40)
    c: InternalAlignment(g42,g40)
    c: Weight(g43) = 1
    c: Equal(g43,g44)
    c: Equal(g43,g45)
    c: InternalAlignment(g43,g46)
    c: InternalAlignment(g44,g46)
    c: InternalAlignment(g45,g46)
    c: InternalAlignment(g47,g46)
    c: InternalAlignment(g48,g46)
    c: Block(g40)
    c: Block(g46)
    c: Coincident(g49,g4)
    c: Coincident(g49,g3)
    c: Horizontal(g49)
    c: Distance(g49) = 450
    c: Coincident(g50,g4)
    c: Coincident(g50,g3)
    c: Horizontal(g50)
    c: Horizontal(g51)
    c: Coincident(g2,g51)
    c: Block(g51)
    c: Coincident(g1,g51)
    c: Weight(g52) = 1
    c: Equal(g52,g53)
    c: Equal(g52,g54)
    c: InternalAlignment(g52,g55)
    c: InternalAlignment(g53,g55)
    c: InternalAlignment(g54,g55)
    c: InternalAlignment(g56,g55)
    c: InternalAlignment(g57,g55)
    c: Block(g55)
    c: Weight(g58) = 1
    c: Equal(g58,g59)
    c: Equal(g58,g60)
    c: InternalAlignment(g58,g61)
    c: InternalAlignment(g59,g61)
    c: InternalAlignment(g60,g61)
    c: InternalAlignment(g62,g61)
    c: InternalAlignment(g63,g61)
    c: Block(g61)
    c: Weight(g64) = 1
    c: Equal(g64,g65)
    c: Equal(g64,g66)
    c: InternalAlignment(g64,g67)
    c: InternalAlignment(g65,g67)
    c: InternalAlignment(g66,g67)
    c: InternalAlignment(g68,g67)
    c: InternalAlignment(g69,g67)
    c: Block(g67)
    c: Weight(g70) = 1
    c: Equal(g70,g71)
    c: Equal(g70,g72)
    c: InternalAlignment(g70,g73)
    c: InternalAlignment(g71,g73)
    c: InternalAlignment(g72,g73)
    c: InternalAlignment(g74,g73)
    c: InternalAlignment(g75,g73)
    c: Block(g73)
    c: Weight(g76) = 1
    c: Equal(g76,g77)
    c: Equal(g76,g78)
    c: InternalAlignment(g76,g79)
    c: InternalAlignment(g77,g79)
    c: InternalAlignment(g78,g79)
    c: InternalAlignment(g80,g79)
    c: InternalAlignment(g81,g79)
    c: Weight(g82) = 1
    c: Equal(g82,g83)
    c: Equal(g82,g84)
    c: InternalAlignment(g82,g85)
    c: InternalAlignment(g83,g85)
    c: InternalAlignment(g84,g85)
    c: InternalAlignment(g86,g85)
    c: InternalAlignment(g87,g85)
    c: Block(g79)
    c: Block(g85)
    c: Coincident(g88,g79)
    c: Coincident(g88,g85)
    c: Vertical(g88)
    c: Coincident(g89,g79)
    c: Coincident(g89,g61)
    c: Coincident(g90,g61)
    c: Coincident(g90,g85)
    c: Weight(g91) = 1
    c: Equal(g91,g92)
    c: Equal(g91,g93)
    c: InternalAlignment(g91,g94)
    c: InternalAlignment(g92,g94)
    c: InternalAlignment(g93,g94)
    c: InternalAlignment(g95,g94)
    c: InternalAlignment(g96,g94)
    c: Weight(g97) = 1
    c: Equal(g97,g98)
    c: Equal(g97,g99)
    c: InternalAlignment(g97,g100)
    c: InternalAlignment(g98,g100)
    c: InternalAlignment(g99,g100)
    c: InternalAlignment(g101,g100)
    c: InternalAlignment(g102,g100)
    c: Block(g94)
    c: Block(g100)
    c: Coincident(g103,g94)
    c: Coincident(g103,g100)
    c: Vertical(g103)
    c: Coincident(g104,g94)
    c: Coincident(g104,g55)
    c: Coincident(g105,g55)
    c: Coincident(g105,g100)
    c: Weight(g106) = 1
    c: Equal(g106,g107)
    c: Equal(g106,g108)
    c: InternalAlignment(g106,g109)
    c: InternalAlignment(g107,g109)
    c: InternalAlignment(g108,g109)
    c: InternalAlignment(g110,g109)
    c: InternalAlignment(g111,g109)
    c: Weight(g112) = 1
    c: Equal(g112,g113)
    c: Equal(g112,g114)
    c: InternalAlignment(g112,g115)
    c: InternalAlignment(g113,g115)
    c: InternalAlignment(g114,g115)
    c: InternalAlignment(g116,g115)
    c: InternalAlignment(g117,g115)
    c: Block(g109)
    c: Block(g115)
    c: Coincident(g118,g109)
    c: Coincident(g118,g115)
    c: Vertical(g118)
    c: Coincident(g119,g115)
    c: Coincident(g119,g73)
    c: Coincident(g120,g73)
    c: Coincident(g120,g109)
    c: Weight(g121) = 1
    c: Equal(g121,g122)
    c: Equal(g121,g123)
    c: InternalAlignment(g121,g124)
    c: InternalAlignment(g122,g124)
    c: InternalAlignment(g123,g124)
    c: InternalAlignment(g125,g124)
    c: InternalAlignment(g126,g124)
    c: Weight(g127) = 1
    c: Equal(g127,g128)
    c: Equal(g127,g129)
    c: InternalAlignment(g127,g130)
    c: InternalAlignment(g128,g130)
    c: InternalAlignment(g129,g130)
    c: InternalAlignment(g131,g130)
    c: InternalAlignment(g132,g130)
    c: Block(g124)
    c: Block(g130)
    c: Coincident(g133,g124)
    c: Coincident(g133,g130)
    c: Vertical(g133)
    c: Coincident(g134,g130)
    c: Coincident(g134,g67)
    c: Coincident(g135,g67)
    c: Coincident(g135,g124)
    c: Weight(g136) = 1
    c: Equal(g136,g137)
    c: Equal(g136,g138)
    c: InternalAlignment(g136,g139)
    c: InternalAlignment(g137,g139)
    c: InternalAlignment(g138,g139)
    c: InternalAlignment(g140,g139)
    c: InternalAlignment(g141,g139)
    c: Weight(g142) = 1
    c: Equal(g142,g143)
    c: Equal(g142,g144)
    c: InternalAlignment(g142,g145)
    c: InternalAlignment(g143,g145)
    c: InternalAlignment(g144,g145)
    c: InternalAlignment(g146,g145)
    c: InternalAlignment(g147,g145)
    c: Weight(g148) = 1
    c: Equal(g148,g149)
    c: Equal(g148,g150)
    c: InternalAlignment(g148,g151)
    c: InternalAlignment(g149,g151)
    c: InternalAlignment(g150,g151)
    c: InternalAlignment(g152,g151)
    c: InternalAlignment(g153,g151)
    c: Weight(g154) = 1
    c: Equal(g154,g155)
    c: Equal(g154,g156)
    c: InternalAlignment(g154,g157)
    c: InternalAlignment(g155,g157)
    c: InternalAlignment(g156,g157)
    c: InternalAlignment(g158,g157)
    c: InternalAlignment(g159,g157)
    c: Block(g157)
    c: Block(g151)
    c: Block(g145)
    c: Block(g139)
    c: Coincident(g160,g34)
    c: Coincident(g160,g157)
    c: Coincident(g161,g157)
    c: Coincident(g161,g151)
    c: Horizontal(g161)
    c: Coincident(g162,g151)
    c: Coincident(g162,g34)
    c: Vertical(g162)
    c: Coincident(g163,g28)
    c: Coincident(g163,g145)
    c: Vertical(g163)
    c: Coincident(g164,g145)
    c: Coincident(g164,g139)
    c: Horizontal(g164)
    c: Coincident(g165,g139)
    c: Coincident(g165,g28)
    c: Weight(g166) = 1
    c: Equal(g166,g167)
    c: Equal(g166,g168)
    c: InternalAlignment(g166,g169)
    c: InternalAlignment(g167,g169)
    c: InternalAlignment(g168,g169)
    c: InternalAlignment(g170,g169)
    c: InternalAlignment(g171,g169)
    c: Weight(g172) = 1
    c: Equal(g172,g173)
    c: Equal(g172,g174)
    c: InternalAlignment(g172,g175)
    c: InternalAlignment(g173,g175)
    c: InternalAlignment(g174,g175)
    c: InternalAlignment(g176,g175)
    c: InternalAlignment(g177,g175)
    c: Weight(g178) = 1
    c: Equal(g178,g179)
    c: Equal(g178,g180)
    c: InternalAlignment(g178,g181)
    c: InternalAlignment(g179,g181)
    c: InternalAlignment(g180,g181)
    c: InternalAlignment(g182,g181)
    c: InternalAlignment(g183,g181)
    c: Weight(g184) = 1
    c: Equal(g184,g185)
    c: Equal(g184,g186)
    c: InternalAlignment(g184,g187)
    c: InternalAlignment(g185,g187)
    c: InternalAlignment(g186,g187)
    c: InternalAlignment(g188,g187)
    c: InternalAlignment(g189,g187)
    c: Block(g187)
    c: Block(g181)
    c: Block(g175)
    c: Block(g169)
    c: Coincident(g190,g187)
    c: Coincident(g190,g181)
    c: Horizontal(g190)
    c: Coincident(g191,g181)
    c: Coincident(g191,g16)
    c: Vertical(g191)
    c: Coincident(g192,g22)
    c: Coincident(g192,g175)
    c: Vertical(g192)
    c: Coincident(g193,g175)
    c: Coincident(g193,g169)
    c: Horizontal(g193)
    c: Coincident(g194,g169)
    c: Coincident(g194,g22)
    c: Coincident(g195,g16)
    c: Weight(g196) = 1
    c: Equal(g196,g197)
    c: Equal(g196,g198)
    c: InternalAlignment(g196,g199)
    c: InternalAlignment(g197,g199)
    c: InternalAlignment(g198,g199)
    c: InternalAlignment(g200,g199)
    c: InternalAlignment(g201,g199)
    c: Weight(g202) = 1
    c: Equal(g202,g203)
    c: Equal(g202,g204)
    c: InternalAlignment(g202,g205)
    c: InternalAlignment(g203,g205)
    c: InternalAlignment(g204,g205)
    c: InternalAlignment(g206,g205)
    c: InternalAlignment(g207,g205)
    c: Block(g205)
    c: Block(g199)
    c: Coincident(g208,g205)
    c: Coincident(g208,g40)
    c: Coincident(g209,g40)
    c: Coincident(g209,g199)
    c: Coincident(g210,g199)
    c: Coincident(g210,g205)
    c: Vertical(g210)
    c: Weight(g211) = 1
    c: Equal(g211,g212)
    c: Equal(g211,g213)
    c: InternalAlignment(g211,g214)
    c: InternalAlignment(g212,g214)
    c: InternalAlignment(g213,g214)
    c: InternalAlignment(g215,g214)
    c: InternalAlignment(g216,g214)
    c: Weight(g217) = 1
    c: Equal(g217,g218)
    c: Equal(g217,g219)
    c: InternalAlignment(g217,g220)
    c: InternalAlignment(g218,g220)
    c: InternalAlignment(g219,g220)
    c: InternalAlignment(g221,g220)
    c: InternalAlignment(g222,g220)
    c: Block(g220)
    c: Block(g214)
    c: Coincident(g223,g214)
    c: Coincident(g223,g46)
    c: Coincident(g224,g46)
    c: Coincident(g224,g220)
    c: Coincident(g225,g220)
    c: Coincident(g225,g214)
    c: Vertical(g225)
    c: Horizontal(g226)
    c: Block(g226)
    c: Vertical(g227)
    c: Block(g227)
    c: Block(g228)
    c: Weight(g229) = 1
    c: Equal(g229,g230)
    c: Equal(g229,g231)
    c: InternalAlignment(g229,g232)
    c: InternalAlignment(g230,g232)
    c: InternalAlignment(g231,g232)
    c: InternalAlignment(g233,g232)
    c: InternalAlignment(g234,g232)
    c: Weight(g235) = 1
    c: Equal(g235,g236)
    c: Equal(g235,g237)
    c: InternalAlignment(g235,g238)
    c: InternalAlignment(g236,g238)
    c: InternalAlignment(g237,g238)
    c: InternalAlignment(g239,g238)
    c: InternalAlignment(g240,g238)
    c: Weight(g241) = 1
    c: Equal(g241,g242)
    c: Equal(g241,g243)
    c: InternalAlignment(g241,g244)
    c: InternalAlignment(g242,g244)
    c: InternalAlignment(g243,g244)
    c: InternalAlignment(g245,g244)
    c: InternalAlignment(g246,g244)
    c: Weight(g247) = 1
    c: Equal(g247,g248)
    c: Equal(g247,g249)
    c: InternalAlignment(g247,g250)
    c: InternalAlignment(g248,g250)
    c: InternalAlignment(g249,g250)
    c: InternalAlignment(g251,g250)
    c: InternalAlignment(g252,g250)
    c: Block(g232)
    c: Block(g238)
    c: Block(g244)
    c: Block(g250)
    c: Coincident(g253,g238)
    c: Coincident(g253,g232)
    c: Horizontal(g253)
    c: Block(g195)
    c: Weight(g254) = 1
    c: Equal(g254,g255)
    c: Equal(g254,g256)
    c: InternalAlignment(g254,g257)
    c: InternalAlignment(g255,g257)
    c: InternalAlignment(g256,g257)
    c: InternalAlignment(g258,g257)
    c: InternalAlignment(g259,g257)
    c: Weight(g260) = 1
    c: Equal(g260,g261)
    c: Equal(g260,g262)
    c: InternalAlignment(g260,g263)
    c: InternalAlignment(g261,g263)
    c: InternalAlignment(g262,g263)
    c: InternalAlignment(g264,g263)
    c: InternalAlignment(g265,g263)
    c: Weight(g266) = 1
    c: Equal(g266,g267)
    c: Equal(g266,g268)
    c: InternalAlignment(g266,g269)
    c: InternalAlignment(g267,g269)
    c: InternalAlignment(g268,g269)
    c: InternalAlignment(g270,g269)
    c: InternalAlignment(g271,g269)
    c: Weight(g272) = 1
    c: Equal(g272,g273)
    c: Equal(g272,g274)
    c: InternalAlignment(g272,g275)
    c: InternalAlignment(g273,g275)
    c: InternalAlignment(g274,g275)
    c: InternalAlignment(g276,g275)
    c: InternalAlignment(g277,g275)
    c: Block(g257)
    c: Block(g263)
    c: Block(g269)
    c: Block(g275)
    c: Coincident(g278,g269)
    c: Coincident(g278,g275)
    c: Horizontal(g278)
    c: Coincident(g279,g275)
    c: Coincident(g279,g257)
    c: Vertical(g279)
    c: Coincident(g280,g257)
    c: Coincident(g280,g263)
    c: Coincident(g281,g263)
    c: Coincident(g281,g269)
    c: Vertical(g281)
    c: Weight(g282) = 1
    c: Equal(g282,g283)
    c: Equal(g282,g284)
    c: InternalAlignment(g282,g285)
    c: InternalAlignment(g283,g285)
    c: InternalAlignment(g284,g285)
    c: InternalAlignment(g286,g285)
    c: InternalAlignment(g287,g285)
    c: Weight(g288) = 1
    c: Equal(g288,g289)
    c: Equal(g288,g290)
    c: InternalAlignment(g288,g291)
    c: InternalAlignment(g289,g291)
    c: InternalAlignment(g290,g291)
    c: InternalAlignment(g292,g291)
    c: InternalAlignment(g293,g291)
    c: Weight(g294) = 1
    c: Equal(g294,g295)
    c: Equal(g294,g296)
    c: InternalAlignment(g294,g297)
    c: InternalAlignment(g295,g297)
    c: InternalAlignment(g296,g297)
    c: InternalAlignment(g298,g297)
    c: InternalAlignment(g299,g297)
    c: Block(g297)
    c: Block(g291)
    c: Block(g285)
    c: Coincident(g300,g291)
    c: Coincident(g300,g285)
    c: Coincident(g301,g285)
    c: Coincident(g301,g297)
    c: Vertical(g301)
    c: Coincident(g302,g297)
    c: Coincident(g302,g291)
    c: Horizontal(g302)
    c: Weight(g303) = 1
    c: Equal(g303,g304)
    c: InternalAlignment(g303,g305)
    c: InternalAlignment(g304,g305)
    c: InternalAlignment(g306,g305)
    c: InternalAlignment(g307,g305)
    c: Weight(g308) = 1
    c: Equal(g308,g309)
    c: Equal(g308,g310)
    c: InternalAlignment(g308,g311)
    c: InternalAlignment(g309,g311)
    c: InternalAlignment(g310,g311)
    c: InternalAlignment(g312,g311)
    c: InternalAlignment(g313,g311)
    c: Weight(g314) = 1
    c: Equal(g314,g315)
    c: Equal(g314,g316)
    c: InternalAlignment(g314,g317)
    c: InternalAlignment(g315,g317)
    c: InternalAlignment(g316,g317)
    c: InternalAlignment(g318,g317)
    c: InternalAlignment(g319,g317)
    c: Equal(g320,g321)
    c: Equal(g320,g322)
    c: InternalAlignment(g320,g323)
    c: InternalAlignment(g321,g323)
    c: InternalAlignment(g322,g323)
    c: InternalAlignment(g324,g323)
    c: InternalAlignment(g325,g323)
    c: Block(g311)
    c: Block(g317)
    c: Block(g323)
    c: Block(g305)
    c: Coincident(g326,g305)
    c: Coincident(g326,g311)
    c: Horizontal(g326)
    c: Coincident(g327,g311)
    c: Coincident(g327,g317)
    c: Vertical(g327)
    c: Coincident(g328,g317)
    c: Coincident(g328,g323)
    c: Horizontal(g328)
    c: Coincident(g329,g323)
    c: Coincident(g329,g305)
    c: Weight(g330) = 1
    c: Equal(g330,g331)
    c: Equal(g330,g332)
    c: InternalAlignment(g330,g333)
    c: InternalAlignment(g331,g333)
    c: InternalAlignment(g332,g333)
    c: InternalAlignment(g334,g333)
    c: InternalAlignment(g335,g333)
    c: Weight(g336) = 1
    c: Equal(g336,g337)
    c: Equal(g336,g338)
    c: InternalAlignment(g336,g339)
    c: InternalAlignment(g337,g339)
    c: InternalAlignment(g338,g339)
    c: InternalAlignment(g340,g339)
    c: InternalAlignment(g341,g339)
    c: Weight(g342) = 1
    c: Equal(g342,g343)
    c: Equal(g342,g344)
    c: InternalAlignment(g342,g345)
    c: InternalAlignment(g343,g345)
    c: InternalAlignment(g344,g345)
    c: InternalAlignment(g346,g345)
    c: InternalAlignment(g347,g345)
    c: Block(g345)
    c: Block(g339)
    c: Block(g333)
    c: Coincident(g348,g345)
    c: Coincident(g348,g339)
    c: Horizontal(g348)
    c: Coincident(g349,g339)
    c: Coincident(g349,g333)
    c: Vertical(g349)
    c: Coincident(g350,g333)
    c: Coincident(g350,g345)
    c: PointOnObject(g351,g279)
    c: PointOnObject(g351,g281)
    c: Block(g351)
FEATURE [Sketcher::SketchObject] Sketch001
  FullyConstrained = true
  MapMode = 4
  Placement = pos=(0,0,0) rot=(0.57735,0.57735,0.57735;2.0944rad)
  Support = -> [Sketch]
  sketch-geometry (46):
    g0: BSplineCurve PolesCount=3 KnotsCount=2 Degree=2 IsPeriodic=0
    g1: ArcOfCircle CenterX=73.1223 CenterY=-32.291 CenterZ=0 NormalX=0 NormalY=0 NormalZ=1 AngleXU=0 Radius=13 StartAngle=5.92268 EndAngle=9.06428
    g2: ArcOfCircle CenterX=66.7816 CenterY=-49.1439 CenterZ=0 NormalX=0 NormalY=0 NormalZ=1 AngleXU=0 Radius=13 StartAngle=2.78068 EndAngle=5.92131
    g3: ArcOfCircle CenterX=55.9263 CenterY=-78.1807 CenterZ=0 NormalX=0 NormalY=0 NormalZ=1 AngleXU=0 Radius=13 StartAngle=5.92268 EndAngle=9.06428
    g4: ArcOfCircle CenterX=49.5884 CenterY=-95.0342 CenterZ=0 NormalX=0 NormalY=0 NormalZ=1 AngleXU=0 Radius=13 StartAngle=2.78068 EndAngle=5.92131
    g5: ArcOfCircle CenterX=38.7206 CenterY=-124.067 CenterZ=0 NormalX=0 NormalY=0 NormalZ=1 AngleXU=0 Radius=13 StartAngle=5.92268 EndAngle=9.06428
    g6: ArcOfCircle CenterX=32.3875 CenterY=-140.92 CenterZ=0 NormalX=0 NormalY=0 NormalZ=1 AngleXU=0 Radius=13 StartAngle=2.78068 EndAngle=5.92131
    g7: ArcOfCircle CenterX=21.4715 CenterY=-169.934 CenterZ=0 NormalX=0 NormalY=0 NormalZ=1 AngleXU=0 Radius=13 StartAngle=5.92268 EndAngle=9.06428
    g8: ArcOfCircle CenterX=15.1336 CenterY=-186.787 CenterZ=0 NormalX=0 NormalY=0 NormalZ=1 AngleXU=0 Radius=13 StartAngle=2.78068 EndAngle=5.92131
    g9-g12: Circle x4 (B-spline internal-alignment scaffolding for g13; pole/knot coordinates omitted)
    g13: BSplineCurve PolesCount=4 KnotsCount=2 Degree=3 IsPeriodic=0
    g14: GeomPoint X=28.8094 Y=-19.0875 Z=0
    g15: GeomPoint X=47.0443 Y=-50.4712 Z=0
    g16: Circle CenterX=53.5586 CenterY=-23.2695 CenterZ=0 NormalX=0 NormalY=0 NormalZ=1 AngleXU=0 Radius=3.24518
    g17: Circle CenterX=-195.441 CenterY=-127.082 CenterZ=0 NormalX=0 NormalY=0 NormalZ=1 AngleXU=0 Radius=1
    g18: Circle CenterX=-8.24091 CenterY=-197.481 CenterZ=0 NormalX=0 NormalY=0 NormalZ=1 AngleXU=0 Radius=1
    g19: Circle CenterX=12.8789 CenterY=-141.321 CenterZ=0 NormalX=0 NormalY=0 NormalZ=1 AngleXU=0 Radius=1
    g20: BSplineCurve PolesCount=3 KnotsCount=2 Degree=2 IsPeriodic=0
    g21: GeomPoint X=-195.441 Y=-127.082 Z=0
    g22: GeomPoint X=12.8789 Y=-141.321 Z=0
    g23: Circle CenterX=-12.8016 CenterY=-179.036 CenterZ=0 NormalX=0 NormalY=0 NormalZ=1 AngleXU=0 Radius=10.5072
    g24: Circle CenterX=0.933922 CenterY=-166.43 CenterZ=0 NormalX=0 NormalY=0 NormalZ=1 AngleXU=0 Radius=3.26661
    g25: Circle CenterX=-33.5518 CenterY=-176.44 CenterZ=0 NormalX=0 NormalY=0 NormalZ=1 AngleXU=0 Radius=5.64388
    g26: Circle CenterX=-47.2366 CenterY=-173.859 CenterZ=0 NormalX=0 NormalY=0 NormalZ=1 AngleXU=0 Radius=3.01653
    g27: Circle CenterX=-56.2595 CenterY=-171.456 CenterZ=0 NormalX=0 NormalY=0 NormalZ=1 AngleXU=0 Radius=2.12826
    g28: ArcOfCircle CenterX=51.2151 CenterY=-198.473 CenterZ=0 NormalX=0 NormalY=0 NormalZ=1 AngleXU=0 Radius=20 StartAngle=2.78189 EndAngle=4.35269
    g29: LineSegment StartX=32.4951 StartY=-191.433 StartZ=0 EndX=94.6578 EndY=-26.1352 EndZ=0
    g30: LineSegment StartX=43.1192 StartY=-220.001 StartZ=0 EndX=-196.497 EndY=-129.89 EndZ=0
    g31: LineSegment StartX=43.1192 StartY=-220.001 StartZ=0 EndX=44.1752 EndY=-217.193 EndZ=0
    g32: LineSegment StartX=117.223 StartY=-19.0875 StartZ=0 EndX=117.223 EndY=-16.0875 EndZ=0
    g33: LineSegment StartX=117.223 StartY=-16.0875 StartZ=0 EndX=17.2232 EndY=-16.0875 EndZ=0
    g34: LineSegment StartX=17.2232 StartY=-16.0875 StartZ=0 EndX=17.2232 EndY=-19.0875 EndZ=0
    g35: LineSegment StartX=28.8094 StartY=-19.0875 StartZ=0 EndX=17.2232 EndY=-19.0875 EndZ=0
    g36: LineSegment StartX=47.0443 StartY=-50.4712 StartZ=0 EndX=12.8789 EndY=-141.321 EndZ=0
    g37: LineSegment StartX=-195.441 StartY=-127.082 StartZ=0 EndX=-196.497 EndY=-129.89 EndZ=0
    g38: LineSegment StartX=85.2866 StartY=-36.8766 StartZ=0 EndX=78.9396 EndY=-53.7463 EndZ=0
    g39: LineSegment StartX=60.9579 StartY=-27.7053 StartZ=0 EndX=54.6191 EndY=-44.5532 EndZ=0
    g40: LineSegment StartX=68.0907 StartY=-82.7664 StartZ=0 EndX=61.7465 EndY=-99.6365 EndZ=0
    g41: LineSegment StartX=43.7619 StartY=-73.595 StartZ=0 EndX=37.426 EndY=-90.4435 EndZ=0
    g42: LineSegment StartX=50.885 StartY=-128.652 StartZ=0 EndX=44.5456 EndY=-145.522 EndZ=0
    g43: LineSegment StartX=26.5562 StartY=-119.481 StartZ=0 EndX=20.2251 EndY=-136.329 EndZ=0
    g44: LineSegment StartX=9.3071 StartY=-165.349 StartZ=0 EndX=2.97115 EndY=-182.197 EndZ=0
    g45: LineSegment StartX=33.6358 StartY=-174.52 StartZ=0 EndX=27.2917 EndY=-191.39 EndZ=0
  constraints (71):
    c: Block(g0)
    c: Block(g1)
    c: Block(g2)
    c: Block(g4)
    c: Block(g3)
    c: Block(g6)
    c: Block(g5)
    c: Block(g8)
    c: Block(g7)
    c: Weight(g9) = 1
    c: Equal(g9,g10)
    c: Equal(g9,g11)
    c: Equal(g9,g12)
    c: InternalAlignment(g9-g12 -> g13) x4
    c: InternalAlignment(g14,g13)
    c: InternalAlignment(g15,g13)
    c: Block(g16)
    c: Weight(g17) = 1
    c: Equal(g17,g18)
    c: Equal(g17,g19)
    c: InternalAlignment(g17,g20)
    c: InternalAlignment(g18,g20)
    c: InternalAlignment(g19,g20)
    c: InternalAlignment(g21,g20)
    c: InternalAlignment(g22,g20)
    c: Block(g20)
    c: Block(g23)
    c: Block(g24)
    c: Block(g25)
    c: Block(g26)
    c: Block(g27)
    c: Block(g28)
    c: Coincident(g29,g28)
    c: Coincident(g29,g0)
    c: Block(g13)
    c: Coincident(g31,g30)
    c: Coincident(g31,g28)
    c: Block(g31)
    c: Coincident(g32,g0)
    c: Vertical(g32)
    c: Coincident(g33,g32)
    c: Horizontal(g33)
    c: Coincident(g34,g33)
    c: Vertical(g34)
    c: Block(g33)
    c: Coincident(g35,g13)
    c: Coincident(g35,g34)
    c: Horizontal(g35)
    c: Coincident(g36,g13)
    c: Coincident(g36,g20)
    c: Coincident(g37,g20)
    c: Coincident(g37,g30)
    c: Block(g30)
    c: Coincident(g38,g1)
    c: Coincident(g38,g2)
    c: Coincident(g39,g1)
    c: Coincident(g39,g2)
    c: Coincident(g40,g3)
    c: Coincident(g40,g4)
    c: Coincident(g41,g3)
    c: Coincident(g41,g4)
    c: Coincident(g42,g5)
    c: Coincident(g42,g6)
    c: Coincident(g43,g5)
    c: Coincident(g43,g6)
    c: Coincident(g44,g7)
    c: Coincident(g44,g8)
    c: Coincident(g45,g7)
    c: Coincident(g45,g8)
    c: Distance(g30) = 256
    c: Distance(g33) = 100
FEATURE [Part::Extrusion] Extrude002
  Base = -> Sketch001
  Dir = (1,0,0)
  DirMode = 2
  FaceMakerClass = Part::FaceMakerBullseye
  LengthFwd = 8
  LengthRev = 0
  Solid = true
  Symmetric = false
FEATURE [Sketcher::SketchObject] Sketch002
  FullyConstrained = true
  sketch-geometry (20):
    g0: LineSegment StartX=-2.77179 StartY=-200.304 StartZ=0 EndX=5.22821 EndY=-200.304 EndZ=0
    g1: LineSegment StartX=5.22821 StartY=-200.304 StartZ=0 EndX=5.22821 EndY=-197.304 EndZ=0
    g2: LineSegment StartX=-2.77179 StartY=-200.304 StartZ=0 EndX=-2.77179 EndY=-197.304 EndZ=0
    g3: LineSegment StartX=5.22821 StartY=-197.304 StartZ=0 EndX=8.22821 EndY=-197.304 EndZ=0
    g4: LineSegment StartX=-2.77179 StartY=-197.304 StartZ=0 EndX=-5.77179 EndY=-197.304 EndZ=0
    g5: LineSegment StartX=19.2282 StartY=-203.304 StartZ=0 EndX=19.2282 EndY=-206.304 EndZ=0
    g6: LineSegment StartX=-16.7718 StartY=-203.304 StartZ=0 EndX=-16.7718 EndY=-206.304 EndZ=0
    g7: LineSegment StartX=-16.7718 StartY=-206.304 StartZ=0 EndX=19.2282 EndY=-206.304 EndZ=0
    g8: Circle CenterX=-16.7718 CenterY=-203.304 CenterZ=0 NormalX=0 NormalY=0 NormalZ=1 AngleXU=0 Radius=1
    g9: Circle CenterX=-5.77179 CenterY=-203.304 CenterZ=0 NormalX=0 NormalY=0 NormalZ=1 AngleXU=0 Radius=1
    g10: Circle CenterX=-5.77179 CenterY=-197.304 CenterZ=0 NormalX=0 NormalY=0 NormalZ=1 AngleXU=0 Radius=1
    g11: BSplineCurve PolesCount=3 KnotsCount=2 Degree=2 IsPeriodic=0
    g12: GeomPoint X=-16.7718 Y=-203.304 Z=0
    g13: GeomPoint X=-5.77179 Y=-197.304 Z=0
    g14: Circle CenterX=19.2282 CenterY=-203.304 CenterZ=0 NormalX=0 NormalY=0 NormalZ=1 AngleXU=0 Radius=1
    g15: Circle CenterX=8.22821 CenterY=-203.304 CenterZ=0 NormalX=0 NormalY=0 NormalZ=1 AngleXU=0 Radius=1
    g16: Circle CenterX=8.22821 CenterY=-197.304 CenterZ=0 NormalX=0 NormalY=0 NormalZ=1 AngleXU=0 Radius=1
    g17: BSplineCurve PolesCount=3 KnotsCount=2 Degree=2 IsPeriodic=0
    g18: GeomPoint X=19.2282 Y=-203.304 Z=0
    g19: GeomPoint X=8.22821 Y=-197.304 Z=0
  constraints (41):
    c: Horizontal(g0)
    c: Distance(g0) = 8
    c: Coincident(g1,g0)
    c: Vertical(g1)
    c: Distance(g1) = 3
    c: Coincident(g2,g0)
    c: Vertical(g2)
    c: Distance(g2) = 3
    c: Coincident(g3,g1)
    c: Horizontal(g3)
    c: Distance(g3) = 3
    c: Coincident(g4,g2)
    c: Horizontal(g4)
    c: Distance(g4) = 3
    c: Vertical(g5)
    c: Vertical(g6)
    c: Coincident(g7,g6)
    c: Coincident(g7,g5)
    c: Weight(g8) = 1
    c: Equal(g8,g9)
    c: Equal(g8,g10)
    c: Coincident(g11,g4)
    c: InternalAlignment(g8,g11)
    c: InternalAlignment(g9,g11)
    c: InternalAlignment(g10,g11)
    c: InternalAlignment(g12,g11)
    c: InternalAlignment(g13,g11)
    c: Coincident(g17,g5)
    c: Weight(g14) = 1
    c: Equal(g14,g15)
    c: Equal(g14,g16)
    c: Coincident(g17,g3)
    c: InternalAlignment(g14,g17)
    c: InternalAlignment(g15,g17)
    c: InternalAlignment(g16,g17)
    c: InternalAlignment(g18,g17)
    c: InternalAlignment(g19,g17)
    c: Block(g7)
    c: Block(g17)
    c: Block(g11)
    c: Block(g6)
FEATURE [Part::Extrusion] Extrude003
  Base = -> Sketch002
  Dir = (0,0,1)
  DirMode = 2
  FaceMakerClass = Part::FaceMakerBullseye
  LengthFwd = 260
  LengthRev = 0
  Solid = true
  Symmetric = false
FEATURE [Part::Extrusion] Extrude
  Base = -> Sketch
  Dir = (0,0,1)
  DirMode = 2
  FaceMakerClass = Part::FaceMakerBullseye
  LengthFwd = 14
  LengthRev = 0
  Solid = true
  Symmetric = false
